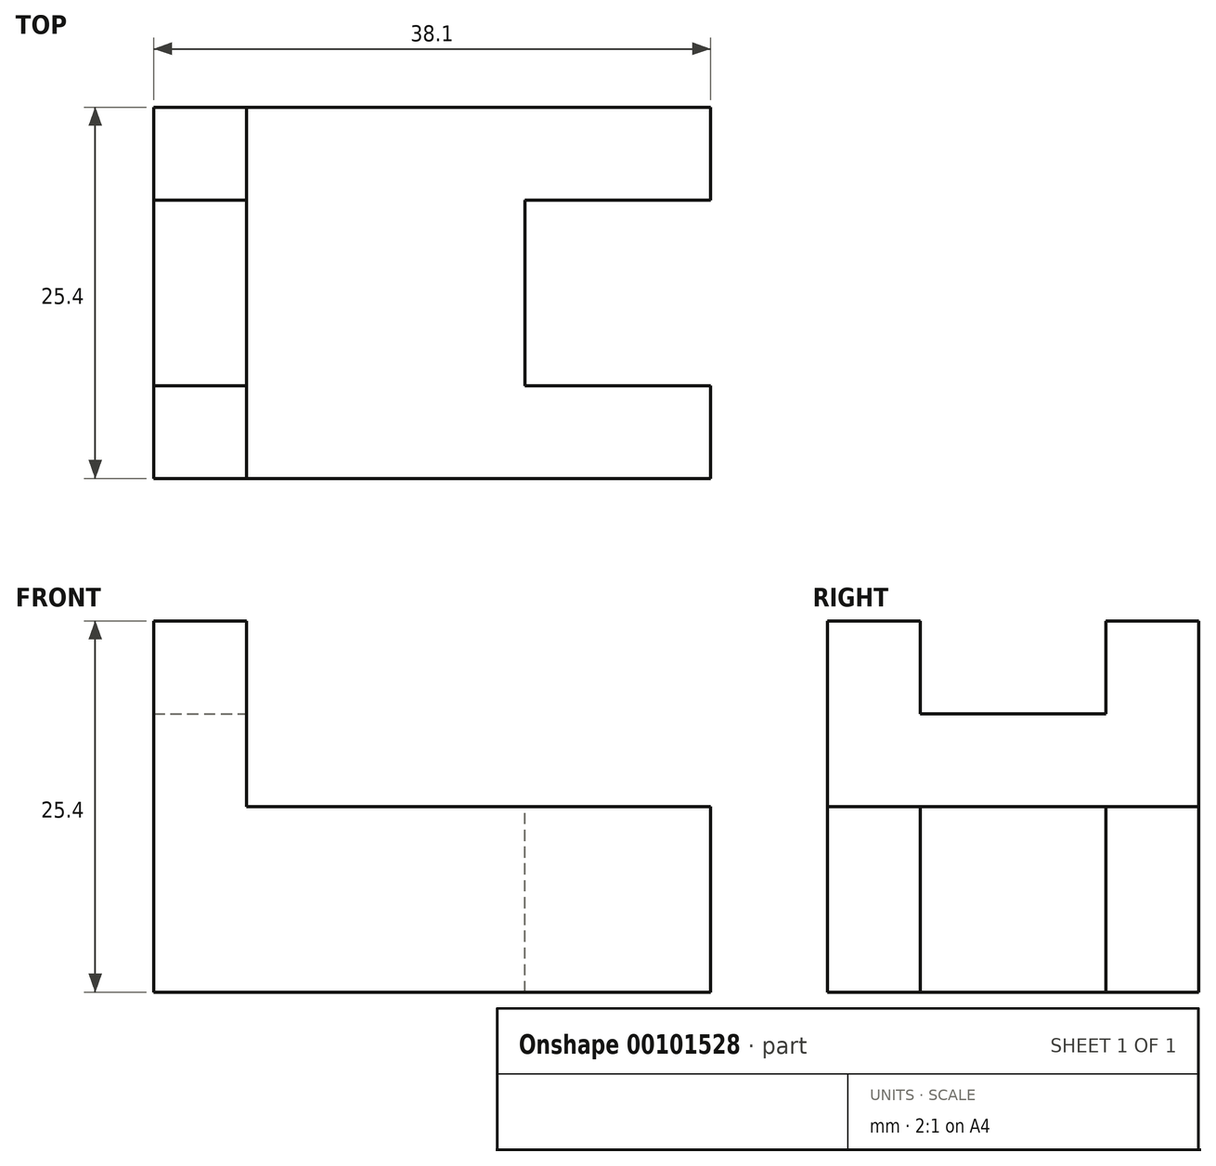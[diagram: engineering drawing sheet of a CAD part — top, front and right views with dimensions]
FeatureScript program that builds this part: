
annotation { "Feature Type Name" : "Feature", "Feature Type Description" : "" }
export const myFeature = defineFeature(function(context is Context, id is Id, definition is map)
    precondition{}
    {
        {
            var Q0;
            Q0=qCreatedBy(makeId("Front.planeOp"),FACE);
            var sketch = newSketch(context, id + "F0", { "sketchPlane" : qUnion([Q0])});
            skLineSegment(sketch, "E0", {"start": v(0, 0) * mm, "end": v(0, 25.4) * mm});
            skLineSegment(sketch, "E1", {"start": v(0, 25.4) * mm, "end": v(6.35, 25.4) * mm});
            skLineSegment(sketch, "E2", {"start": v(6.35, 25.4) * mm, "end": v(6.35, 12.7) * mm});
            skLineSegment(sketch, "E3", {"start": v(6.35, 12.7) * mm, "end": v(38.1, 12.7) * mm});
            skLineSegment(sketch, "E4", {"start": v(38.1, 12.7) * mm, "end": v(38.1, 0) * mm});
            skLineSegment(sketch, "E5", {"start": v(38.1, 0) * mm, "end": v(0, 0) * mm});
            skSolve(sketch);
        }
        {
            var Q0;
            Q0 = qSketchRegion(id + "F0", true);
            extrude(context, id + "F1", {"entities" : qUnion([Q0]), "depth" : 25.4 * mm});
        }
        {
            var Q0;
            Q0=makeQuery(id+"F1.opExtrude","SWEPT_FACE",FACE,{"disambiguationData":[OSD([sQuery(id+"F0.wireOp",EDGE,"E4")])]});
            var sketch = newSketch(context, id + "F2", { "sketchPlane" : qUnion([Q0])});
            skLineSegment(sketch, "E6", {"start": v(-19.05, 0) * mm, "end": v(-6.35, 0) * mm});
            skLineSegment(sketch, "E7", {"start": v(-6.35, 0) * mm, "end": v(-6.35, 12.7) * mm});
            skLineSegment(sketch, "E8", {"start": v(-6.35, 12.7) * mm, "end": v(-19.05, 12.7) * mm});
            skLineSegment(sketch, "E9", {"start": v(-19.05, 12.7) * mm, "end": v(-19.05, 0) * mm});
            skSolve(sketch);
        }
        {
            var Q0;
            Q0 = qSketchRegion(id + "F2", true);
            extrude(context, id + "F3", {"entities" : qUnion([Q0]), "operationType" : NewBodyOperationType.REMOVE, "oppositeDirection" : true, "depth" : 12.7 * mm});
        }
        {
            var Q0;
            Q0=makeQuery(id+"F1.opExtrude","SWEPT_FACE",FACE,{"disambiguationData":[OSD([sQuery(id+"F0.wireOp",EDGE,"E2")])]});
            var sketch = newSketch(context, id + "F4", { "sketchPlane" : qUnion([Q0])});
            skLineSegment(sketch, "E10", {"start": v(-19.05, 25.4) * mm, "end": v(-19.05, 19.05) * mm});
            skPoint(sketch, "E10.endSnap0", {"position": v(-25.4, 19.05) * mm});
            skLineSegment(sketch, "E11", {"start": v(-19.05, 19.05) * mm, "end": v(-6.35, 19.05) * mm});
            skLineSegment(sketch, "E12", {"start": v(-6.35, 19.05) * mm, "end": v(-6.35, 25.4) * mm});
            skLineSegment(sketch, "E13", {"start": v(-6.35, 25.4) * mm, "end": v(-19.05, 25.4) * mm});
            skSolve(sketch);
        }
        {
            var Q0;
            Q0 = qSketchRegion(id + "F4", true);
            extrude(context, id + "F5", {"entities" : qUnion([Q0]), "operationType" : NewBodyOperationType.REMOVE, "oppositeDirection" : true, "depth" : 6.35 * mm});
        }
    });
